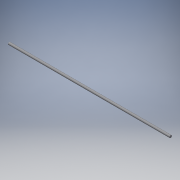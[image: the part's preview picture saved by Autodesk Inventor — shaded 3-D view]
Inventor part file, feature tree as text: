
AUTODESK INVENTOR PART (.ipt)
format: ipt  version: 2016 (Build 200138000, 138)  size: 114,176 bytes
history: native  units: mm
features: extrude x4, sketch x4
ambient origin geometry x8: Origin, YZ Plane, XZ Plane, XY Plane, X Axis, Y Axis, Z Axis, Center Point
bodies: Solid1 (feature_tree)
feature tree (8):
  extrude  "Extrusion1"  Depth=1300.0mm TaperAngle=0.0deg
  extrude  "Extrusion2"  Depth=1300.0mm TaperAngle=0.0deg
  extrude  "Extrusion3"  Depth=1300.0mm TaperAngle=0.0deg
  extrude  "Extrusion4"  [1 undecoded]
  sketch  "Sketch1"  dims[d0=20.0mm d1=1300.0mm d2=0.0mm]
  sketch  "Sketch2"  dims[d5=15.0mm d6=1300.0mm d7=0.0mm]
  sketch  "Sketch4"  dims[d8=1300.0mm d9=0.0mm d10=1300.0mm d11=0.0mm]
  sketch  "Sketch5"
note: 1 required parameter value undecoded (feature->parameter linkage not recoverable at this tier; creation-order binding heuristic only, values carry confidence <= 0.55)
